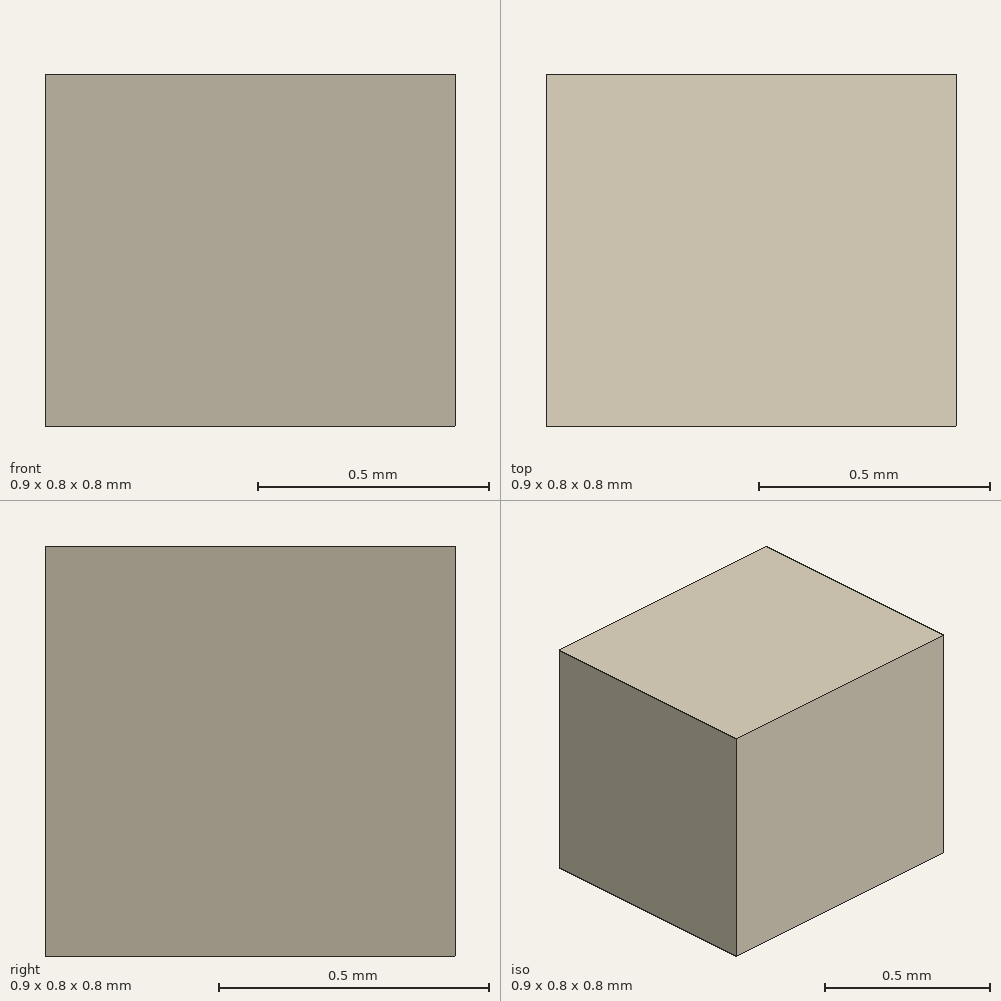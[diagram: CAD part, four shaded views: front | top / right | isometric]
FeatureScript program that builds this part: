
annotation { "Feature Type Name" : "Feature", "Feature Type Description" : "" }
export const myFeature = defineFeature(function(context is Context, id is Id, definition is map)
    precondition{}
    {
        {
            var Q0;
            Q0=qCreatedBy(makeId("Top.planeOp"),FACE);
            var sketch = newSketch(context, id + "F0", { "sketchPlane" : qUnion([Q0])});
            skLineSegment(sketch, "E0.bottom", {"start": v(0.44, -0.38) * mm, "end": v(-0.44, -0.38) * mm});
            skLineSegment(sketch, "E0.top", {"start": v(0.44, 0.38) * mm, "end": v(-0.44, 0.38) * mm});
            skLineSegment(sketch, "E0.left", {"start": v(0.44, -0.38) * mm, "end": v(0.44, 0.38) * mm});
            skLineSegment(sketch, "E0.right", {"start": v(-0.44, -0.38) * mm, "end": v(-0.44, 0.38) * mm});
            skPoint(sketch, "E0.middle", {"position": v(0, 0) * mm});
            skSolve(sketch);
        }
        {
            var Q0;
            Q0=makeQuery(id+"F0.imprint","IMPRINT",FACE,{"disambiguationData":[TD([[makeQuery(id+"F0.imprint","IMPRINT",EDGE,{"derivedFrom":sQuery(id+"F0.wireOp",EDGE,"E0.bottom")}),-1.0]])]});
            extrude(context, id + "F1", {"entities" : qUnion([Q0]), "depth" : 0.76 * mm, "offsetDistance" : 25.4 * mm});
        }
    });
